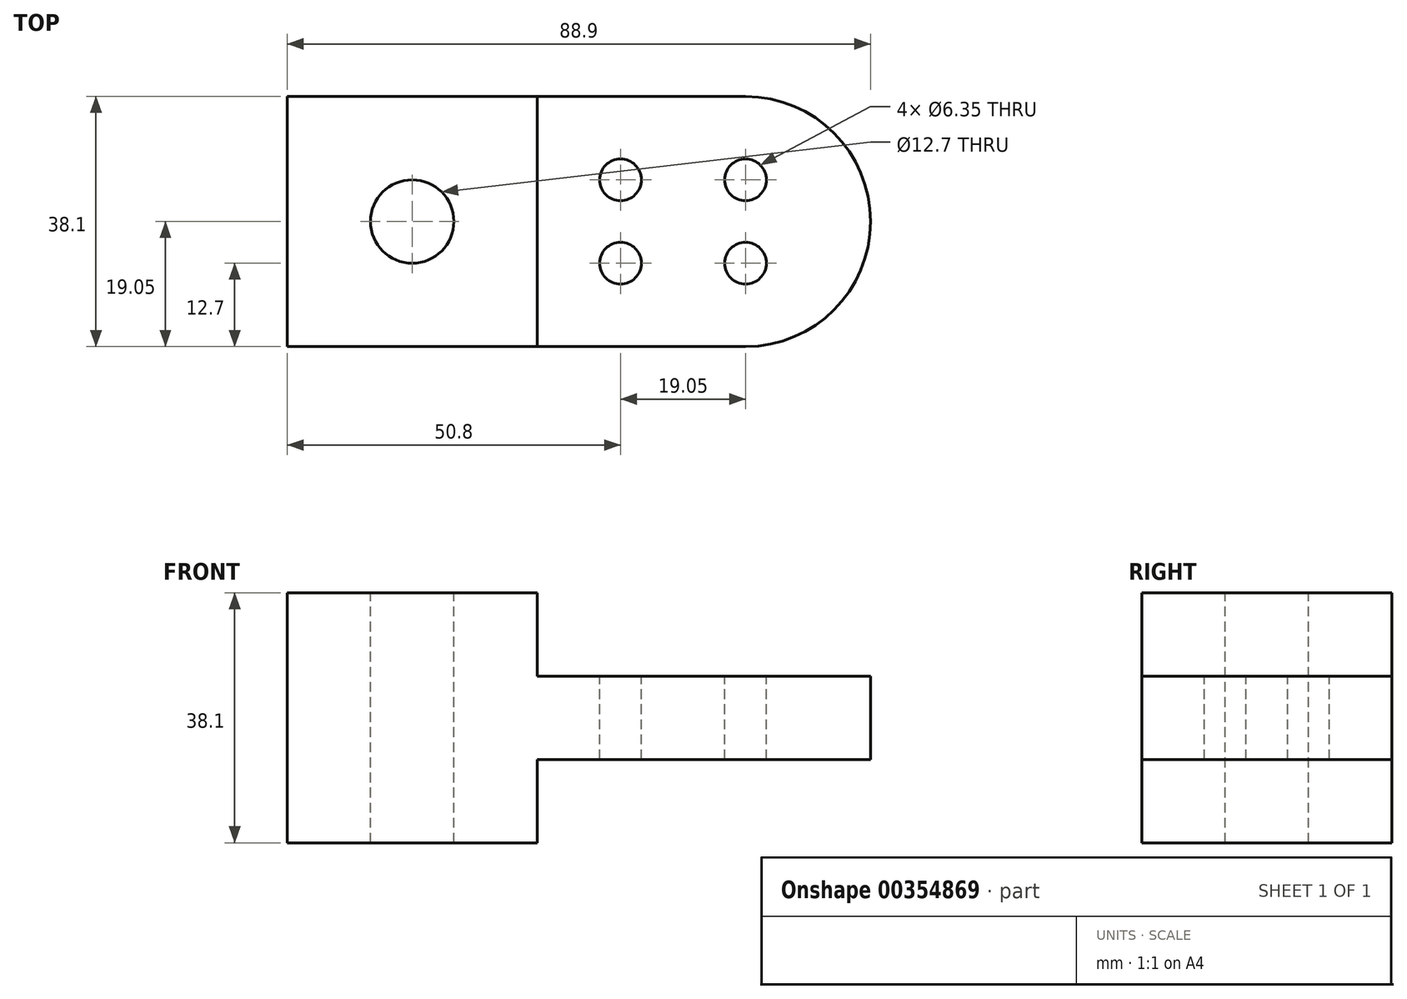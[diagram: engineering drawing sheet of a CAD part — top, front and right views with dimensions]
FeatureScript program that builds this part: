
annotation { "Feature Type Name" : "Feature", "Feature Type Description" : "" }
export const myFeature = defineFeature(function(context is Context, id is Id, definition is map)
    precondition{}
    {
        {
            var Q0;
            Q0=qCreatedBy(makeId("Top.planeOp"),FACE);
            var sketch = newSketch(context, id + "F0", { "sketchPlane" : qUnion([Q0])});
            skLineSegment(sketch, "E0.bottom", {"start": v(0, 0) * mm, "end": v(38.1, 0) * mm});
            skLineSegment(sketch, "E0.top", {"start": v(0, 38.1) * mm, "end": v(38.1, 38.1) * mm});
            skLineSegment(sketch, "E0.left", {"start": v(0, 0) * mm, "end": v(0, 38.1) * mm});
            skLineSegment(sketch, "E0.right", {"start": v(38.1, 0) * mm, "end": v(38.1, 38.1) * mm});
            skSolve(sketch);
        }
        {
            var Q0;
            Q0 = qSketchRegion(id + "F0", true);
            extrude(context, id + "F1", {"entities" : qUnion([Q0]), "endBound" : BoundingType.SYMMETRIC, "depth" : 38.1 * mm});
        }
        {
            var Q0;
            Q0=qCreatedBy(makeId("Top.planeOp"),FACE);
            var sketch = newSketch(context, id + "F2", { "sketchPlane" : qUnion([Q0])});
            skLineSegment(sketch, "E1.bottom", {"start": v(38.1, 0) * mm, "end": v(69.85, 0) * mm});
            skLineSegment(sketch, "E1.top", {"start": v(38.1, 38.1) * mm, "end": v(69.85, 38.1) * mm});
            skLineSegment(sketch, "E1.left", {"start": v(38.1, 0) * mm, "end": v(38.1, 38.1) * mm});
            skLineSegment(sketch, "E1.right", {"start": v(69.85, 0) * mm, "end": v(69.85, 38.1) * mm});
            skSolve(sketch);
        }
        {
            var Q0;
            Q0 = qSketchRegion(id + "F2", true);
            extrude(context, id + "F3", {"entities" : qUnion([Q0]), "operationType" : NewBodyOperationType.ADD, "endBound" : BoundingType.SYMMETRIC, "depth" : 12.7 * mm});
        }
        {
            var Q0;
            Q0=qCreatedBy(makeId("Top.planeOp"),FACE);
            var sketch = newSketch(context, id + "F4", { "sketchPlane" : qUnion([Q0])});
            skArc(sketch, "E2", {"start": v(69.85, 0) * mm, "mid": v(88.9, 19.05) * mm, "end": v(69.85, 38.1) * mm});
            skLineSegment(sketch, "E3", {"start": v(69.85, 38.1) * mm, "end": v(69.85, 0) * mm});
            skSolve(sketch);
        }
        {
            var Q0;
            Q0 = qSketchRegion(id + "F4", true);
            extrude(context, id + "F5", {"entities" : qUnion([Q0]), "operationType" : NewBodyOperationType.ADD, "endBound" : BoundingType.SYMMETRIC, "depth" : 12.7 * mm});
        }
        {
            var Q0;
            Q0=makeQuery(id+"F1.opExtrude","CAP_FACE",FACE,{"disambiguationData":[OSD([sQuery(id+"F0.wireOp",EDGE,"E0.bottom"),sQuery(id+"F0.wireOp",EDGE,"E0.top"),sQuery(id+"F0.wireOp",EDGE,"E0.left"),sQuery(id+"F0.wireOp",EDGE,"E0.right")])],"isStart":false});
            var sketch = newSketch(context, id + "F6", { "sketchPlane" : qUnion([Q0])});
            skCircle(sketch, "E4", {"center": v(19.05, 19.05) * mm, "radius": 6.35 * mm});
            skSolve(sketch);
        }
        {
            var Q0;
            Q0 = qSketchRegion(id + "F6", true);
            extrude(context, id + "F7", {"entities" : qUnion([Q0]), "operationType" : NewBodyOperationType.REMOVE, "endBound" : BoundingType.THROUGH_ALL, "oppositeDirection" : true, "depth" : 25.4 * mm});
        }
        {
            var Q0;
            Q0=makeQuery(id+"F5.boolean.opBoolean","MERGE",FACE,{"derivedFrom":[makeQuery(id+"F3.opExtrude","CAP_FACE",FACE,{"disambiguationData":[OSD([sQuery(id+"F2.wireOp",EDGE,"E1.bottom"),sQuery(id+"F2.wireOp",EDGE,"E1.top"),sQuery(id+"F2.wireOp",EDGE,"E1.left"),sQuery(id+"F2.wireOp",EDGE,"E1.right")])],"isStart":false}),makeQuery(id+"F5.opExtrude","CAP_FACE",FACE,{"disambiguationData":[OSD([sQuery(id+"F4.wireOp",EDGE,"E2"),sQuery(id+"F4.wireOp",EDGE,"E3")])],"isStart":false})]});
            var sketch = newSketch(context, id + "F8", { "sketchPlane" : qUnion([Q0])});
            skLineSegment(sketch, "E5", {"start": v(40.5, 25.4) * mm, "end": v(85.02, 25.4) * mm, "construction": true});
            skLineSegment(sketch, "E6", {"start": v(40.5, 12.7) * mm, "end": v(85.02, 12.7) * mm, "construction": true});
            skLineSegment(sketch, "E7", {"start": v(69.85, 38.1) * mm, "end": v(69.85, 0) * mm, "construction": true});
            skLineSegment(sketch, "E8", {"start": v(50.8, 38.1) * mm, "end": v(50.8, 0) * mm, "construction": true});
            skCircle(sketch, "E9", {"center": v(50.8, 25.4) * mm, "radius": 3.18 * mm});
            skCircle(sketch, "E10", {"center": v(69.85, 25.4) * mm, "radius": 3.18 * mm});
            skCircle(sketch, "E11", {"center": v(69.85, 12.7) * mm, "radius": 3.18 * mm});
            skCircle(sketch, "E12", {"center": v(50.8, 12.7) * mm, "radius": 3.18 * mm});
            skSolve(sketch);
        }
        {
            var Q0;
            Q0 = qSketchRegion(id + "F8", true);
            extrude(context, id + "F9", {"entities" : qUnion([Q0]), "operationType" : NewBodyOperationType.REMOVE, "endBound" : BoundingType.THROUGH_ALL, "oppositeDirection" : true, "depth" : 25.4 * mm});
        }
    });
